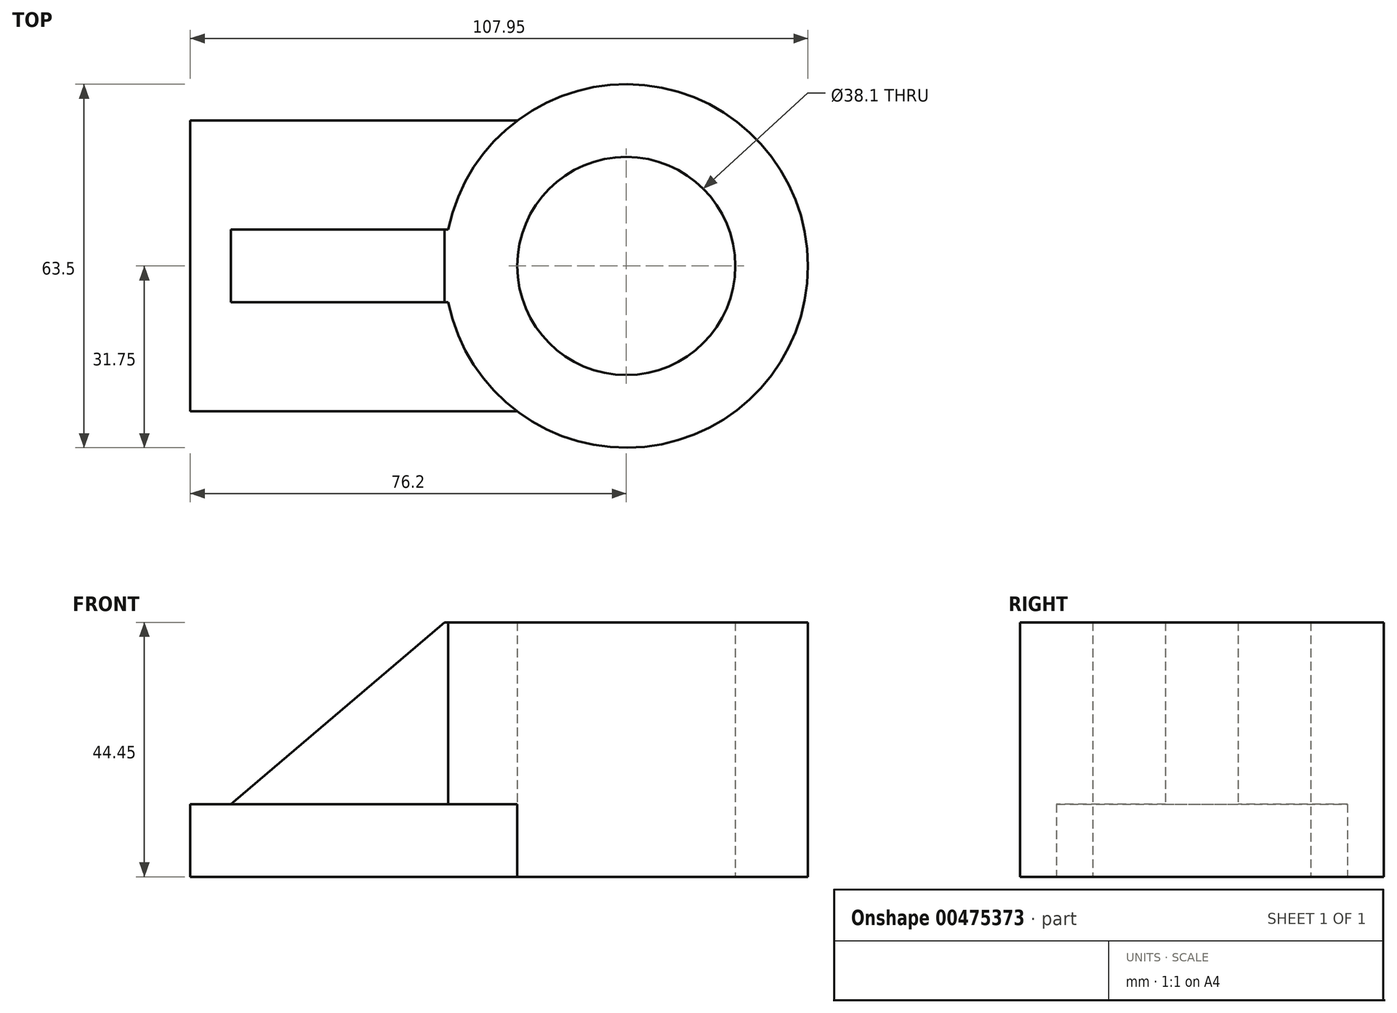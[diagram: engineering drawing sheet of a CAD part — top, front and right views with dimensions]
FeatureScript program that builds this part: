
annotation { "Feature Type Name" : "Feature", "Feature Type Description" : "" }
export const myFeature = defineFeature(function(context is Context, id is Id, definition is map)
    precondition{}
    {
        {
            var Q0;
            Q0=qCreatedBy(makeId("Top.planeOp"),FACE);
            var sketch = newSketch(context, id + "F0", { "sketchPlane" : qUnion([Q0])});
            skLineSegment(sketch, "E0.bottom", {"start": v(19.05, -25.4) * mm, "end": v(-38.1, -25.4) * mm});
            skLineSegment(sketch, "E0.top", {"start": v(19.05, 25.4) * mm, "end": v(-38.1, 25.4) * mm});
            skLineSegment(sketch, "E0.right", {"start": v(-38.1, -25.4) * mm, "end": v(-38.1, 25.4) * mm});
            skPoint(sketch, "E0.middle", {"position": v(0, 0) * mm});
            skCircle(sketch, "E1", {"center": v(38.1, 0) * mm, "radius": 31.75 * mm});
            skCircle(sketch, "E2", {"center": v(38.1, 0) * mm, "radius": 19.05 * mm});
            skSolve(sketch);
        }
        {
            var Q0;
            {var subQ0=sQuery(id+"F0.wireOp",EDGE,"E0.bottom");Q0=makeQuery(id+"F0.imprint","IMPRINT",FACE,{"disambiguationData":[TD([[makeQuery(id+"F0.imprint","IMPRINT",EDGE,{"derivedFrom":subQ0}),-1.0]])]});}
            extrude(context, id + "F1", {"entities" : qUnion([Q0]), "depth" : 12.7 * mm});
        }
        {
            var Q0;
            Q0=makeQuery(id+"F0.imprint","IMPRINT",FACE,{"disambiguationData":[TD([[makeQuery(id+"F0.imprint","IMPRINT",EDGE,{"derivedFrom":sQuery(id+"F0.wireOp",EDGE,"E2")}),-1.0]])]});
            extrude(context, id + "F2", {"entities" : qUnion([Q0]), "operationType" : NewBodyOperationType.ADD, "depth" : 44.45 * mm});
        }
        {
            var Q0;
            Q0=qCreatedBy(makeId("Front.planeOp"),FACE);
            var sketch = newSketch(context, id + "F3", { "sketchPlane" : qUnion([Q0])});
            skLineSegment(sketch, "E3", {"start": v(19.05, 0) * mm, "end": v(19.05, 44.45) * mm});
            skLineSegment(sketch, "E4", {"start": v(57.15, 44.45) * mm, "end": v(57.15, 0) * mm});
            skLineSegment(sketch, "E5.0.0", {"start": v(19.05, 12.7) * mm, "end": v(6.35, 12.7) * mm});
            skLineSegment(sketch, "E5.0.1", {"start": v(19.05, 12.7) * mm, "end": v(-38.1, 12.7) * mm});
            skLineSegment(sketch, "E5.0.3", {"start": v(-38.1, 12.7) * mm, "end": v(19.05, 12.7) * mm});
            skLineSegment(sketch, "E6", {"start": v(6.35, 12.7) * mm, "end": v(6.35, 44.45) * mm, "construction": true});
            skLineSegment(sketch, "E7", {"start": v(19.05, 44.45) * mm, "end": v(6.35, 44.45) * mm});
            skLineSegment(sketch, "E8", {"start": v(6.35, 44.45) * mm, "end": v(-31.01, 12.7) * mm});
            skSolve(sketch);
        }
        {
            var Q0;
            {var subQ0=sQuery(id+"F3.wireOp",EDGE,"E7");Q0=makeQuery(id+"F3.imprint","IMPRINT",FACE,{"disambiguationData":[TD([[makeQuery(id+"F3.imprint","IMPRINT",EDGE,{"derivedFrom":subQ0}),1.0]])]});}
            extrude(context, id + "F4", {"entities" : qUnion([Q0]), "operationType" : NewBodyOperationType.ADD, "endBound" : BoundingType.SYMMETRIC, "depth" : 12.7 * mm});
        }
    });
